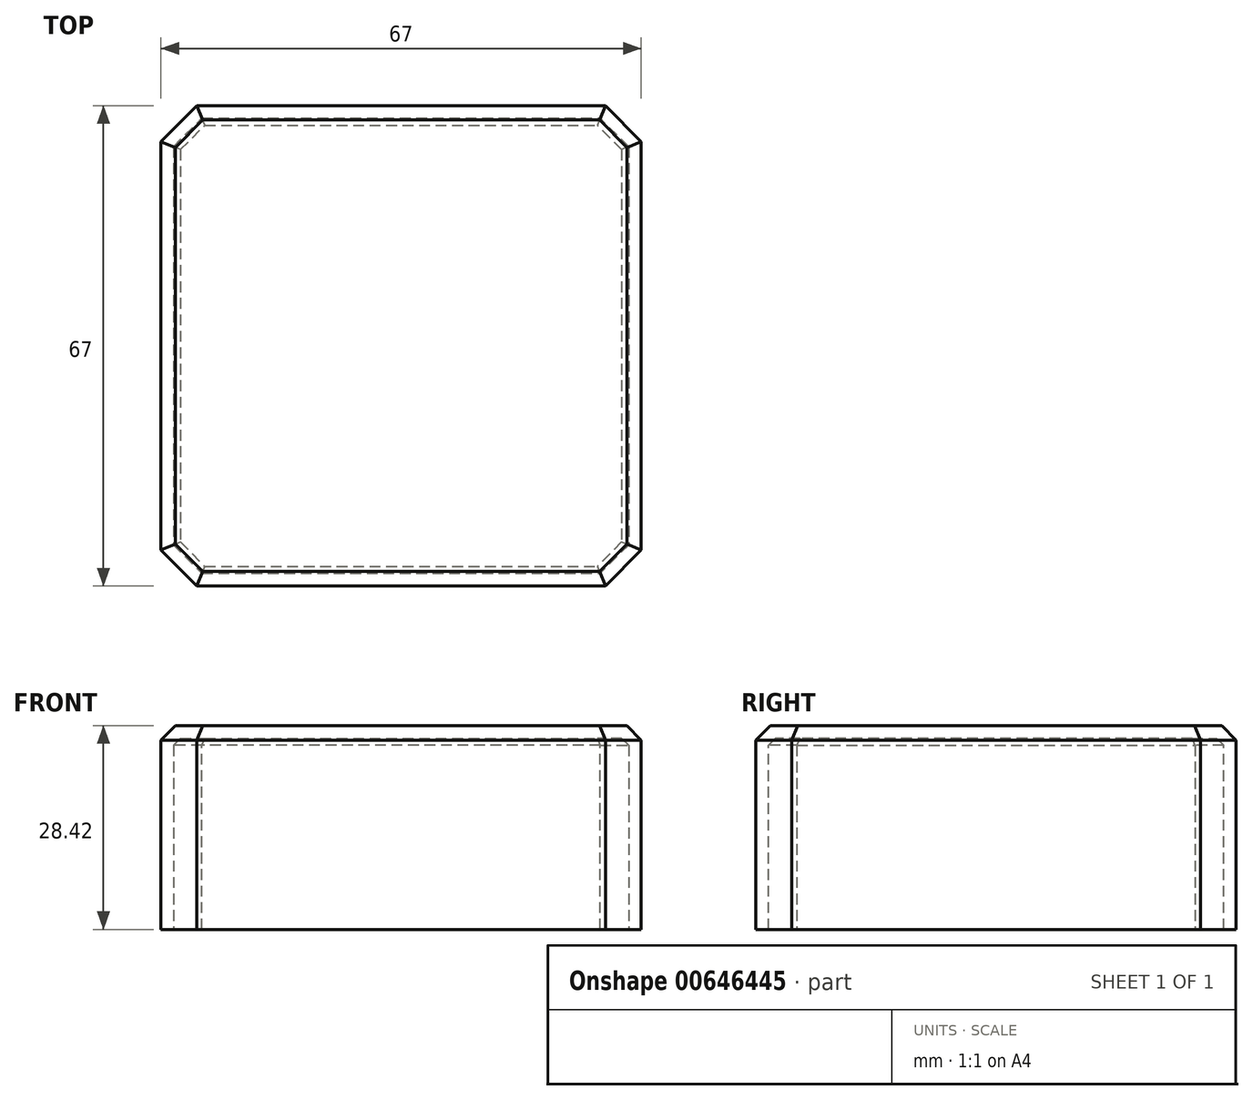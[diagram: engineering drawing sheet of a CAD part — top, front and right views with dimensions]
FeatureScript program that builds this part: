
annotation { "Feature Type Name" : "Feature", "Feature Type Description" : "" }
export const myFeature = defineFeature(function(context is Context, id is Id, definition is map)
    precondition{}
    {
        {
            var Q0;
            Q0=qCreatedBy(makeId("Top.planeOp"),FACE);
            var sketch = newSketch(context, id + "F0", { "sketchPlane" : qUnion([Q0])});
            skLineSegment(sketch, "E0.bottom", {"start": v(-42.55, 31.06) * mm, "end": v(24.45, 31.06) * mm});
            skLineSegment(sketch, "E0.top", {"start": v(-42.55, -35.94) * mm, "end": v(24.45, -35.94) * mm});
            skLineSegment(sketch, "E0.left", {"start": v(-42.55, 31.06) * mm, "end": v(-42.55, -35.94) * mm});
            skLineSegment(sketch, "E0.right", {"start": v(24.45, 31.06) * mm, "end": v(24.45, -35.94) * mm});
            skSolve(sketch);
        }
        {
            var Q0;
            Q0 = qSketchRegion(id + "F0", true);
            extrude(context, id + "F1", {"entities" : qUnion([Q0]), "depth" : 28.42 * mm, "offsetDistance" : 25 * mm});
        }
        {
            var Q0;
            Q0=makeQuery(id+"F1.opExtrude","SWEPT_EDGE",EDGE,{"disambiguationData":[OSD([sQuery(id+"F0.wireOp",EDGE,"E0.top"),sQuery(id+"F0.wireOp",EDGE,"E0.left")])]});
            var Q1;
            Q1=makeQuery(id+"F1.opExtrude","SWEPT_EDGE",EDGE,{"disambiguationData":[OSD([sQuery(id+"F0.wireOp",EDGE,"E0.top"),sQuery(id+"F0.wireOp",EDGE,"E0.right")])]});
            var Q2;
            Q2=makeQuery(id+"F1.opExtrude","SWEPT_EDGE",EDGE,{"disambiguationData":[OSD([sQuery(id+"F0.wireOp",EDGE,"E0.bottom"),sQuery(id+"F0.wireOp",EDGE,"E0.right")])]});
            var Q3;
            Q3=makeQuery(id+"F1.opExtrude","SWEPT_EDGE",EDGE,{"disambiguationData":[OSD([sQuery(id+"F0.wireOp",EDGE,"E0.bottom"),sQuery(id+"F0.wireOp",EDGE,"E0.left")])]});
            chamfer(context, id + "F2", {"entities" : qUnion([Q0, Q1, Q2, Q3]), "width" : 5 * mm, "tangentPropagation" : true});
        }
        {
            var Q0;
            Q0=makeQuery(id+"F1.opExtrude","CAP_FACE",FACE,{"disambiguationData":[OSD([sQuery(id+"F0.wireOp",EDGE,"E0.bottom"),sQuery(id+"F0.wireOp",EDGE,"E0.top"),sQuery(id+"F0.wireOp",EDGE,"E0.left"),sQuery(id+"F0.wireOp",EDGE,"E0.right")])],"isStart":false});
            chamfer(context, id + "F3", {"entities" : qUnion([Q0]), "width" : 2 * mm, "tangentPropagation" : true});
        }
        {
            var Q0;
            Q0=makeQuery(id+"F1.opExtrude","CAP_FACE",FACE,{"disambiguationData":[OSD([sQuery(id+"F0.wireOp",EDGE,"E0.bottom"),sQuery(id+"F0.wireOp",EDGE,"E0.top"),sQuery(id+"F0.wireOp",EDGE,"E0.left"),sQuery(id+"F0.wireOp",EDGE,"E0.right")])],"isStart":true});
            shell(context, id + "F4", {"entities" : qUnion([Q0]), "thickness" : 1.75 * mm});
        }
        {
            var Q0;
            Q0=makeQuery(id+"F1.opExtrude","SWEPT_FACE",FACE,{"disambiguationData":[OSD([sQuery(id+"F0.wireOp",EDGE,"E0.top")])]});
            cPlane(context, id + "F5", {"entities" : qUnion([Q0]), "cplaneType" : CPlaneType.OFFSET, "offset" : 0 * mm, "width" : 150 * mm, "height" : 150 * mm});
        }
    });
